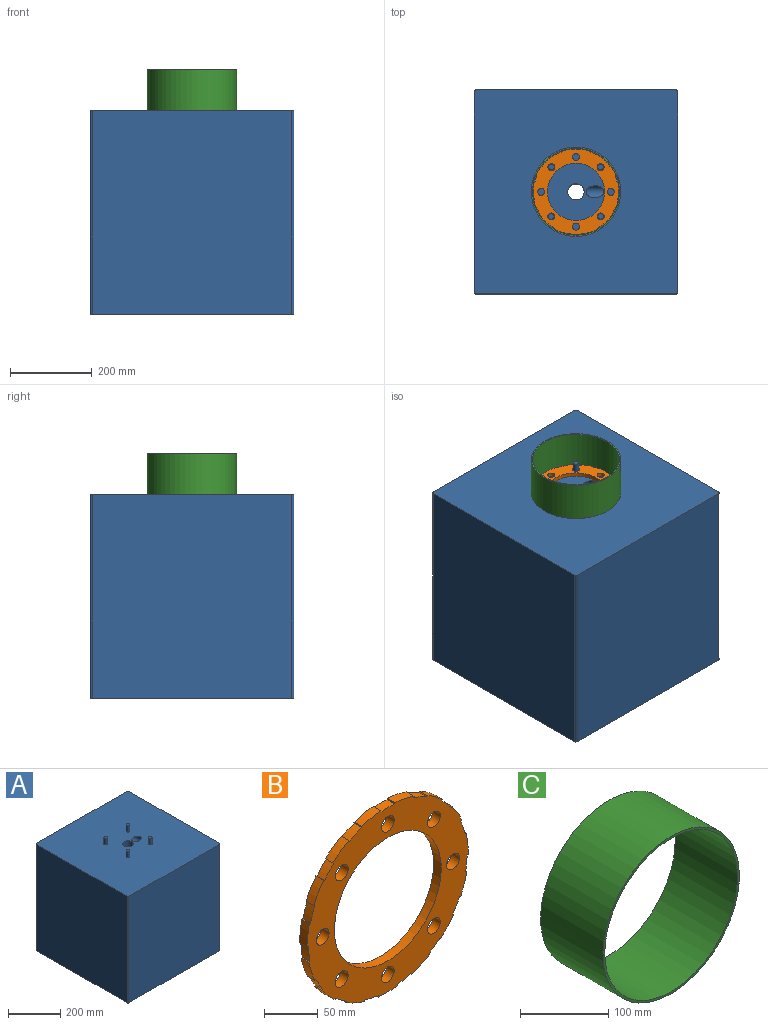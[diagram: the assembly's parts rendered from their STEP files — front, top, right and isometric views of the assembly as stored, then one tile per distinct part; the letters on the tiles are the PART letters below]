
ASSEMBLY  parts=3 mates=2
PART A: 20 faces, bbox 527.5x506.5x536.5 mm
  f0: plane 500x490mm, normal (0,1,0), area 245000mm2, adj f4,f5,f7,f10
  f1: plane 500x490mm, normal (-1,0,0), area 245000mm2, adj f4,f5,f7,f8
  f2: plane 500x490mm, normal (0,-1,0), area 245000mm2, adj f4,f5,f8,f9
  f3: plane 500x490mm, normal (1,0,0), area 244014.3mm2, adj f4,f5,f9,f10,f19
  f4: plane 506.49x506.49mm, normal (0,0,1), area 247092mm2, adj f0,f1,f2,f3,f6,f7,f8,f9
  f5: plane 500x500mm, normal (0,0,-1), area 248721.9mm2, adj f0,f1,f2,f3,f6,f7,f8,f9
  f6: cylinder r=20mm len=500mm, axis (0,0,1), area 62831.9mm2, adj f4,f5
  f7: cylinder r=5mm len=500mm, axis (0,0,1), area 3927mm2, adj f0,f1,f4,f5
  f8: cylinder r=5mm len=500mm, axis (0,0,-1), area 3927mm2, adj f1,f2,f4,f5
  f9: cylinder r=5mm len=500mm, axis (0,0,1), area 3927mm2, adj f2,f3,f4,f5
  f10: cylinder r=5mm len=500mm, axis (0,0,-1), area 3927mm2, adj f0,f3,f4,f5
  f11: cylinder r=7mm len=30mm, axis (0,0,-1), area 1319.5mm2, adj f4,f12
  f12: plane 14x14mm, normal (0,0,1), area 153.9mm2, adj f11
  f13: cylinder r=7mm len=30mm, axis (0,0,-1), area 1319.5mm2, adj f4,f14
  f14: plane 14x14mm, normal (0,0,1), area 153.9mm2, adj f13
  f15: cylinder r=7mm len=30mm, axis (0,0,-1), area 1319.5mm2, adj f4,f16
  f16: plane 14x14mm, normal (0,0,1), area 153.9mm2, adj f15
  f17: cylinder r=7mm len=30mm, axis (0,0,-1), area 1319.5mm2, adj f4,f18
  f18: plane 14x14mm, normal (0,0,1), area 153.9mm2, adj f17
  f19: cylinder r=15mm len=245.98mm, axis (-0.72,0,0.7), area 26733.9mm2, adj f3,f4
PART B: 71 faces, bbox 210.9x10x210.5 mm
  f0: plane 210.9x210.5mm, normal (0,-1,0), area 17312.8mm2, adj f2,f3,f4,f5,f6,f7,f8,f9
  f1: plane 210.9x210.5mm, normal (0,1,0), area 17312.8mm2, adj f2,f3,f4,f5,f6,f7,f8,f9
  f2: cylinder r=105.45mm len=20.79mm, axis (0,1,0), area 257.7mm2, adj f0,f1,f31,f68
  f3: cylinder r=105.45mm len=25.14mm, axis (0,1,0), area 257.7mm2, adj f0,f1,f26,f70
  f4: cylinder r=105.45mm len=25.14mm, axis (0,1,0), area 257.7mm2, adj f0,f1,f28,f65
  f5: cylinder r=105.45mm len=20.79mm, axis (0,1,0), area 257.7mm2, adj f0,f1,f62,f67
  f6: cylinder r=105.45mm len=22.26mm, axis (0,1,0), area 257.7mm2, adj f0,f1,f59,f64
  f7: cylinder r=105.45mm len=25.56mm, axis (0,1,0), area 257.7mm2, adj f0,f1,f56,f61
  f8: cylinder r=105.45mm len=24.44mm, axis (0,1,0), area 257.7mm2, adj f0,f1,f53,f58
  f9: cylinder r=105.45mm len=19.1mm, axis (0,1,0), area 257.7mm2, adj f0,f1,f50,f55
  f10: cylinder r=105.45mm len=23.48mm, axis (0,1,0), area 257.7mm2, adj f0,f1,f47,f52
  f11: cylinder r=105.45mm len=25.7mm, axis (0,1,0), area 257.7mm2, adj f0,f1,f44,f49
  f12: cylinder r=105.45mm len=23.48mm, axis (0,1,0), area 257.7mm2, adj f0,f1,f41,f46
  f13: cylinder r=105.45mm len=19.1mm, axis (0,1,0), area 257.7mm2, adj f0,f1,f38,f43
  f14: cylinder r=105.45mm len=24.44mm, axis (0,1,0), area 257.7mm2, adj f0,f1,f35,f40
  f15: cylinder r=105.45mm len=25.56mm, axis (0,1,0), area 257.7mm2, adj f0,f1,f32,f37
  f16: cylinder r=105.45mm len=22.26mm, axis (0,1,0), area 257.7mm2, adj f0,f1,f29,f34
  f17: cylinder r=8.5mm len=17mm, axis (0,1,0), area 534.1mm2, adj f0,f1
  f18: cylinder r=8.5mm len=17mm, axis (0,1,0), area 534.1mm2, adj f0,f1
  f19: cylinder r=8.5mm len=17mm, axis (0,1,0), area 534.1mm2, adj f0,f1
  f20: cylinder r=8.5mm len=17mm, axis (0,1,0), area 534.1mm2, adj f0,f1
  f21: cylinder r=8.5mm len=17mm, axis (0,1,0), area 534.1mm2, adj f0,f1
  f22: cylinder r=8.5mm len=17mm, axis (0,1,0), area 534.1mm2, adj f0,f1
  f23: cylinder r=8.5mm len=17mm, axis (0,1,0), area 534.1mm2, adj f0,f1
  f24: cylinder r=8.5mm len=17mm, axis (0,1,0), area 534.1mm2, adj f0,f1
  f25: cylinder r=70mm len=140mm, axis (0,1,0), area 4398.2mm2, adj f0,f1
  f26: plane 10x1.49mm, normal (-1,0,0.09), area 15mm2, adj f0,f1,f3,f27
  f27: cylinder r=103.95mm len=18.12mm, axis (0,-1,0), area 181.4mm2, adj f0,f1,f26,f28
  f28: plane 10x1.49mm, normal (1,0,0.09), area 15mm2, adj f0,f1,f4,f27
  f29: plane 10x1.2mm, normal (-0.6,0,0.8), area 15mm2, adj f0,f1,f16,f30
  f30: cylinder r=103.95mm len=13.47mm, axis (0,-1,0), area 181.4mm2, adj f0,f1,f29,f31
  f31: plane 10x1.1mm, normal (0.73,0,-0.68), area 15mm2, adj f0,f1,f2,f30
  f32: plane 10x1.46mm, normal (-0.22,0,0.97), area 15mm2, adj f0,f1,f15,f33
  f33: cylinder r=103.95mm len=17.23mm, axis (0,-1,0), area 181.4mm2, adj f0,f1,f32,f34
  f34: plane 10x1.38mm, normal (0.39,0,-0.92), area 15mm2, adj f0,f1,f16,f33
  f35: plane 10x1.47mm, normal (0.19,0,0.98), area 15mm2, adj f0,f1,f14,f36
  f36: cylinder r=103.95mm len=18.02mm, axis (0,-1,0), area 181.4mm2, adj f0,f1,f35,f37
  f37: plane 10x1.5mm, normal (-0.02,0,-1), area 15mm2, adj f0,f1,f15,f36
  f38: plane 10x1.23mm, normal (0.57,0,0.82), area 15mm2, adj f0,f1,f13,f39
  f39: cylinder r=103.95mm len=15.69mm, axis (0,-1,0), area 181.4mm2, adj f0,f1,f38,f40
  f40: plane 10x1.36mm, normal (-0.42,0,-0.91), area 15mm2, adj f0,f1,f14,f39
  f41: plane 10x1.29mm, normal (0.86,0,0.52), area 15mm2, adj f0,f1,f12,f42
  f42: cylinder r=103.95mm len=14.66mm, axis (0,-1,0), area 181.4mm2, adj f0,f1,f41,f43
  f43: plane 10x1.13mm, normal (-0.75,0,-0.66), area 15mm2, adj f0,f1,f13,f42
  f44: plane 10x1.49mm, normal (0.99,0,0.12), area 15mm2, adj f0,f1,f11,f45
  f45: cylinder r=103.95mm len=17.72mm, axis (0,-1,0), area 181.4mm2, adj f0,f1,f44,f46
  f46: plane 10x1.43mm, normal (-0.96,0,-0.29), area 15mm2, adj f0,f1,f12,f45
  f47: plane 10x1.43mm, normal (0.96,0,-0.29), area 15mm2, adj f0,f1,f10,f48
  f48: cylinder r=103.95mm len=17.72mm, axis (0,-1,0), area 181.4mm2, adj f0,f1,f47,f49
  f49: plane 10x1.49mm, normal (-0.99,0,0.12), area 15mm2, adj f0,f1,f11,f48
  f50: plane 10x1.13mm, normal (0.75,0,-0.66), area 15mm2, adj f0,f1,f9,f51
  f51: cylinder r=103.95mm len=14.66mm, axis (0,-1,0), area 181.4mm2, adj f0,f1,f50,f52
  f52: plane 10x1.29mm, normal (-0.86,0,0.52), area 15mm2, adj f0,f1,f10,f51
  f53: plane 10x1.36mm, normal (0.42,0,-0.91), area 15mm2, adj f0,f1,f8,f54
  f54: cylinder r=103.95mm len=15.69mm, axis (0,-1,0), area 181.4mm2, adj f0,f1,f53,f55
  f55: plane 10x1.23mm, normal (-0.57,0,0.82), area 15mm2, adj f0,f1,f9,f54
  f56: plane 10x1.5mm, normal (0.02,0,-1), area 15mm2, adj f0,f1,f7,f57
  f57: cylinder r=103.95mm len=18.02mm, axis (0,-1,0), area 181.4mm2, adj f0,f1,f56,f58
  f58: plane 10x1.47mm, normal (-0.19,0,0.98), area 15mm2, adj f0,f1,f8,f57
  f59: plane 10x1.38mm, normal (-0.39,0,-0.92), area 15mm2, adj f0,f1,f6,f60
  f60: cylinder r=103.95mm len=17.23mm, axis (0,-1,0), area 181.4mm2, adj f0,f1,f59,f61
  f61: plane 10x1.46mm, normal (0.22,0,0.97), area 15mm2, adj f0,f1,f7,f60
  f62: plane 10x1.1mm, normal (-0.73,0,-0.68), area 15mm2, adj f0,f1,f5,f63
  f63: cylinder r=103.95mm len=13.47mm, axis (0,-1,0), area 181.4mm2, adj f0,f1,f62,f64
  f64: plane 10x1.2mm, normal (0.6,0,0.8), area 15mm2, adj f0,f1,f6,f63
  f65: plane 10x1.42mm, normal (-0.95,0,-0.33), area 15mm2, adj f0,f1,f4,f66
  f66: cylinder r=103.95mm len=16.55mm, axis (0,-1,0), area 181.4mm2, adj f0,f1,f65,f67
  f67: plane 10x1.31mm, normal (0.87,0,0.48), area 15mm2, adj f0,f1,f5,f66
  f68: plane 10x1.31mm, normal (-0.87,0,0.48), area 15mm2, adj f0,f1,f2,f69
  f69: cylinder r=103.95mm len=16.55mm, axis (0,-1,0), area 181.4mm2, adj f0,f1,f68,f70
  f70: plane 10x1.42mm, normal (0.95,0,-0.33), area 15mm2, adj f0,f1,f3,f69
PART C: 4 faces, bbox 219x100x219 mm
  f0: cylinder r=106.5mm len=213mm, axis (0,1,0), area 66915.9mm2, adj f2,f3
  f1: cylinder r=109.5mm len=219mm, axis (0,1,0), area 68800.9mm2, adj f2,f3
  f2: plane 219x219mm, normal (0,-1,0), area 2035.8mm2, adj f0,f1
  f3: plane 219x219mm, normal (0,1,0), area 2035.8mm2, adj f0,f1
PLACE A t=(816.46,-41.95,61.11)mm
PLACE B rot(axis=(-1,0,0),90deg) t=(816.46,-41.95,561.11)mm
PLACE C rot(axis=(-1,0,0),90deg) t=(816.46,-41.95,561.11)mm
MATE fastened B.f2 <-> A.f6  axis (0,0,-1) through (816.46,-41.95,561.11)mm
MATE fastened C.f0 <-> A.f6  axis (0,0,-1) through (816.46,-41.95,561.11)mm
